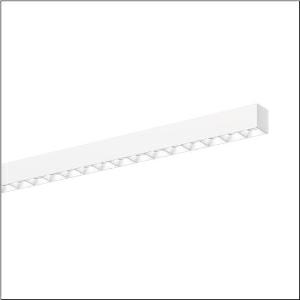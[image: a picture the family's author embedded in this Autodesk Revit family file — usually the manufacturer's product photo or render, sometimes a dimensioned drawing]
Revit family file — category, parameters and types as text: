
# Revit family: silica_r__21_51mx26dc4awb_5f84
name_source: partatom
category: Lighting Fixtures
units: mm (PartAtom-declared; Revit-internal decimal feet)

## family parameters
Cut with Voids When Loaded = No
Host = Face
Light Source = No
Part Type = Normal
Room Calculation Point = No
Round Connector Dimension = Use Diameter
Shared = No

## types (1)
- --- (1 x LED, 10800 lm, 60.6 W, 4000K)
    Apparent Load = 61 VA
    CIE Flux Codes = 83 98 100 100 100
    Color Rendering = 80
    Color Temperature = 4000K
    Default Elevation = 1800 mm
    Description = Silica® 21, office luminaire, primary light control with darklight reflector, of PMMA, white, CAT 2 (L<= 3000cd/m²), light emission: direct distribution, primary light characteristic: symmetric, installation type: surface-mounted, LED, rated luminous flux: 10.800lm, luminous efficacy: 178lm/W, light colour: 840, colour temperature: 4000K, with terminal, 3+2-pole, max. 2.5mm², mains connection: 220..240V, AC, 50/60Hz, rated input power: 60.6W, luminaire housing, of aluminium, traffic white (RAL 9016), length: 3.004mm, width: 53mm, height: 53mm, protection rating (complete): IP20, insulation class (complete): insulation class I (protective earthing), certification: CE, permissible operating ambient temperature: 0..+35°C, standard: EN 50419, packaging unit: 1 piece
    Height = 0 mm  [stored 0 ft]
    Lamp = 1 x LED
    Lamp Light Flux = 10800 lm
    Lamp Power = 60.6 W
    Lamp count = 1
    Length = 3004 mm
    Luminous efficacy = 178 lm/W
    Manufacturer = Siteco
    ModVariant = No
    Model = 51MX26DC4AWB
    Mounting Place = Ceiling
    Mounting Type = Recessed
    Number of Poles = 1
    OnlyDefault = Yes
    Power Factor = 1
    Product Name = Silica® 21
    Product group = office luminaire | ceiling recessed
    ProductGroupID = 401
    Protection Class = Protection class I
    Protection Degree = IP 20
    RLX_Detail_Level = 1
    RLX_Emergency_Light_Flux = 0 lm
    RLX_Emergency_Type = 0
    RLX_Emergency_Type_DB = No
    RlxData = <blob elided: 59417 chars, md5=02878907>
    Socket = socket
    Standby Power = 0 W
    System Light Flux = 10800 lm
    System Power = 61 W
    Type Comments = factory setting: luminous flux: 100 % | dim-lin: 254 | 336 mA
    Type Image = l_1297772.jpg
    URL = http://relux.com
    VarID = @adj_055325
    Voltage = 0 V
    Weight = 0.00 kg
    Width = 53 mm

note: [stored X ft] marks values corroborated as IEEE doubles in the binary element streams (Revit-internal decimal feet)

## geometry (parser evidence)
native form markers: Blend x4, Sweep x10
no freeform markers — native parametric forms only
